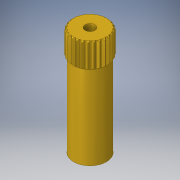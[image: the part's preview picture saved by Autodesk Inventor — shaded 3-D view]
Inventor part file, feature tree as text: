
AUTODESK INVENTOR PART (.ipt)
format: ipt  version: 2021.2 (Build 252289000, 289)  size: 367,104 bytes
history: native  units: mm
features: extrude x6, sketch x6, pattern_circular x2, plane x2, projected_geometry x2, other x1, mirror x1
ambient origin geometry x8: Origin, YZ Plane, XZ Plane, XY Plane, X Axis, Y Axis, Z Axis, Center Point
bodies: Body1 (feature_tree)
feature tree (20):
  other  "Sólido1"
  extrude  "Extrusión1"  Depth=13.5mm TaperAngle=0.0deg
  extrude  "Extrusión2"  Depth=4.0mm TaperAngle=0.0deg
  extrude  "Extrusión3"  Depth=4.0mm TaperAngle=360.0deg
  pattern_circular  "Patrón circular1"  Angle=45.0deg  [1 undecoded]
  plane  "Plano de trabajo1"
  extrude  "Extrusión4"  Depth=13.5mm
  pattern_circular  "Patrón circular2"  [2 undecoded]
  extrude  "Extrusión5"  Depth=13.5mm TaperAngle=360.0deg
  extrude  "Extrusión6"  Depth=13.5mm
  plane  "Plano de trabajo3"
  mirror  "Simetría2"
  sketch  "Boceto1"  dims[d0=5.8mm d1=13.5mm d2=0.0mm]
  sketch  "Boceto2"  dims[d3=0.3mm d4=4.0mm d5=0.0mm]
  projected_geometry  "Contorno proyectado1"
  sketch  "Boceto3"  dims[d9=4.0mm d10=0.0mm d11=260.0mm d12=360.0deg]
  projected_geometry  "Contorno proyectado2"
  sketch  "Boceto5"  dims[d21=0.3mm]
  sketch  "Boceto6"  dims[d22=13.962634mm]
  sketch  "Boceto7"  dims[d23=8.726646mm d25=45.0deg d26=0.25mm d27=0.7mm d28=0.0mm d29=260.0mm d30=360.0deg d32=1.6mm d33=4.0mm d34=0.0mm d36=13.5mm d37=0.0mm d38=5.3mm]
note: 3 required parameter values undecoded (feature->parameter linkage not recoverable at this tier; creation-order binding heuristic only, values carry confidence <= 0.55)
